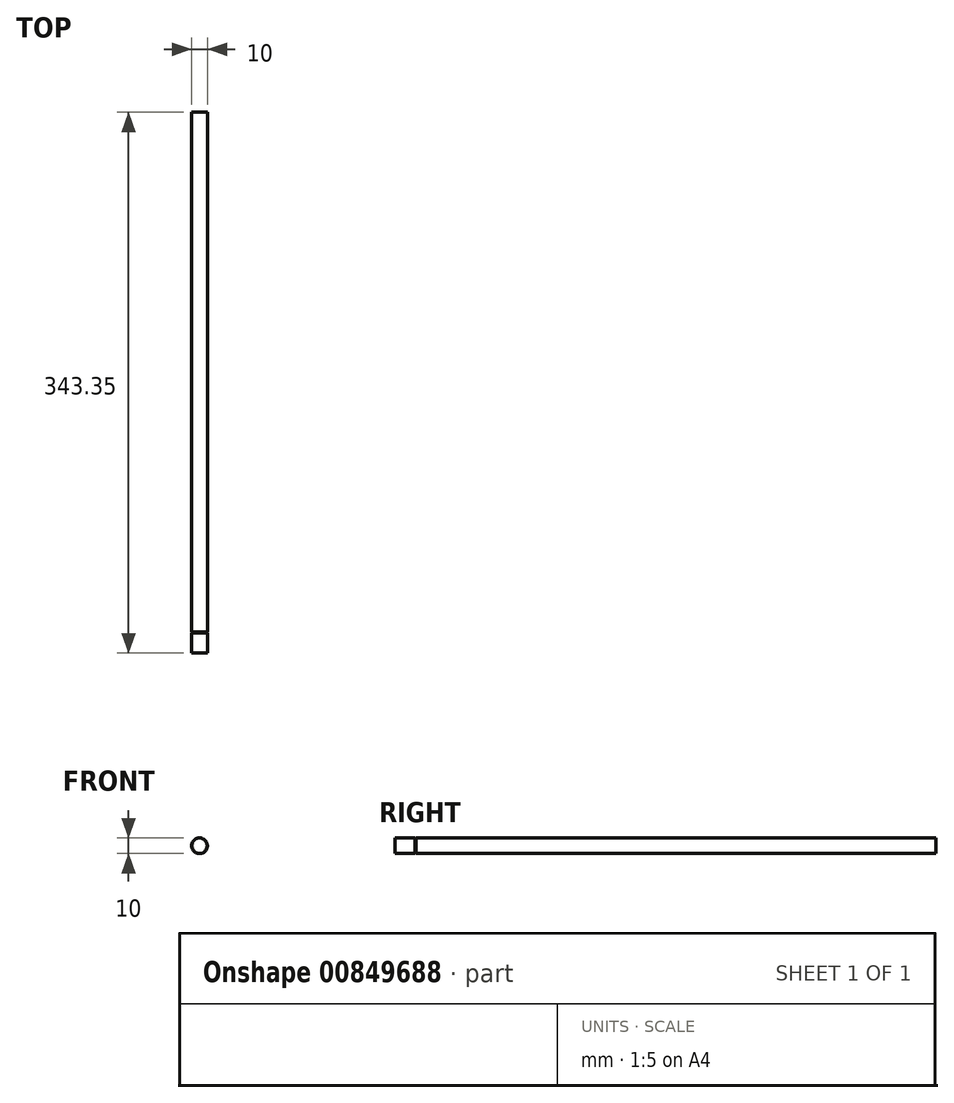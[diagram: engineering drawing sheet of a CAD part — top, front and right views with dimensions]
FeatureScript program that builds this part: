
annotation { "Feature Type Name" : "Feature", "Feature Type Description" : "" }
export const myFeature = defineFeature(function(context is Context, id is Id, definition is map)
    precondition{}
    {
        {
            var Q0;
            Q0=qCreatedBy(makeId("Front.planeOp"),FACE);
            var sketch = newSketch(context, id + "F0", { "sketchPlane" : qUnion([Q0])});
            skCircle(sketch, "E0", {"center": v(0, 0) * mm, "radius": 5 * mm});
            skSolve(sketch);
        }
        {
            var Q0;
            Q0=makeQuery(id+"F0.imprint","IMPRINT",FACE,{"disambiguationData":[TD([[makeQuery(id+"F0.imprint","IMPRINT",EDGE,{"derivedFrom":sQuery(id+"F0.wireOp",EDGE,"E0")}),1.0]])]});
            extrude(context, id + "F1", {"entities" : qUnion([Q0]), "depth" : 330.2 * mm, "offsetDistance" : 25 * mm});
        }
        {
            var Q0;
            Q0=makeQuery(id+"F1.opExtrude","CAP_FACE",FACE,{"disambiguationData":[OSD([sQuery(id+"F0.wireOp",EDGE,"E0")])],"isStart":false});
            var sketch = newSketch(context, id + "F2", { "sketchPlane" : qUnion([Q0])});
            skCircle(sketch, "E1", {"center": v(0, 0) * mm, "radius": 4.32 * mm});
            skSolve(sketch);
        }
        {
            var Q0;
            Q0 = qSketchRegion(id + "F2", true);
            extrude(context, id + "F3", {"entities" : qUnion([Q0]), "operationType" : NewBodyOperationType.ADD, "depth" : .45 * mm, "offsetDistance" : 25 * mm});
        }
        {
            var Q0;
            Q0=makeQuery(id+"F3.opExtrude","CAP_FACE",FACE,{"disambiguationData":[OSD([sQuery(id+"F2.wireOp",EDGE,"E1")])],"isStart":false});
            var sketch = newSketch(context, id + "F4", { "sketchPlane" : qUnion([Q0])});
            skCircle(sketch, "E2", {"center": v(0, 0) * mm, "radius": 5 * mm});
            skSolve(sketch);
        }
        {
            var Q0;
            Q0 = qSketchRegion(id + "F4", true);
            extrude(context, id + "F5", {"entities" : qUnion([Q0]), "operationType" : NewBodyOperationType.ADD, "depth" : 12.7 * mm, "offsetDistance" : 25 * mm});
        }
    });
